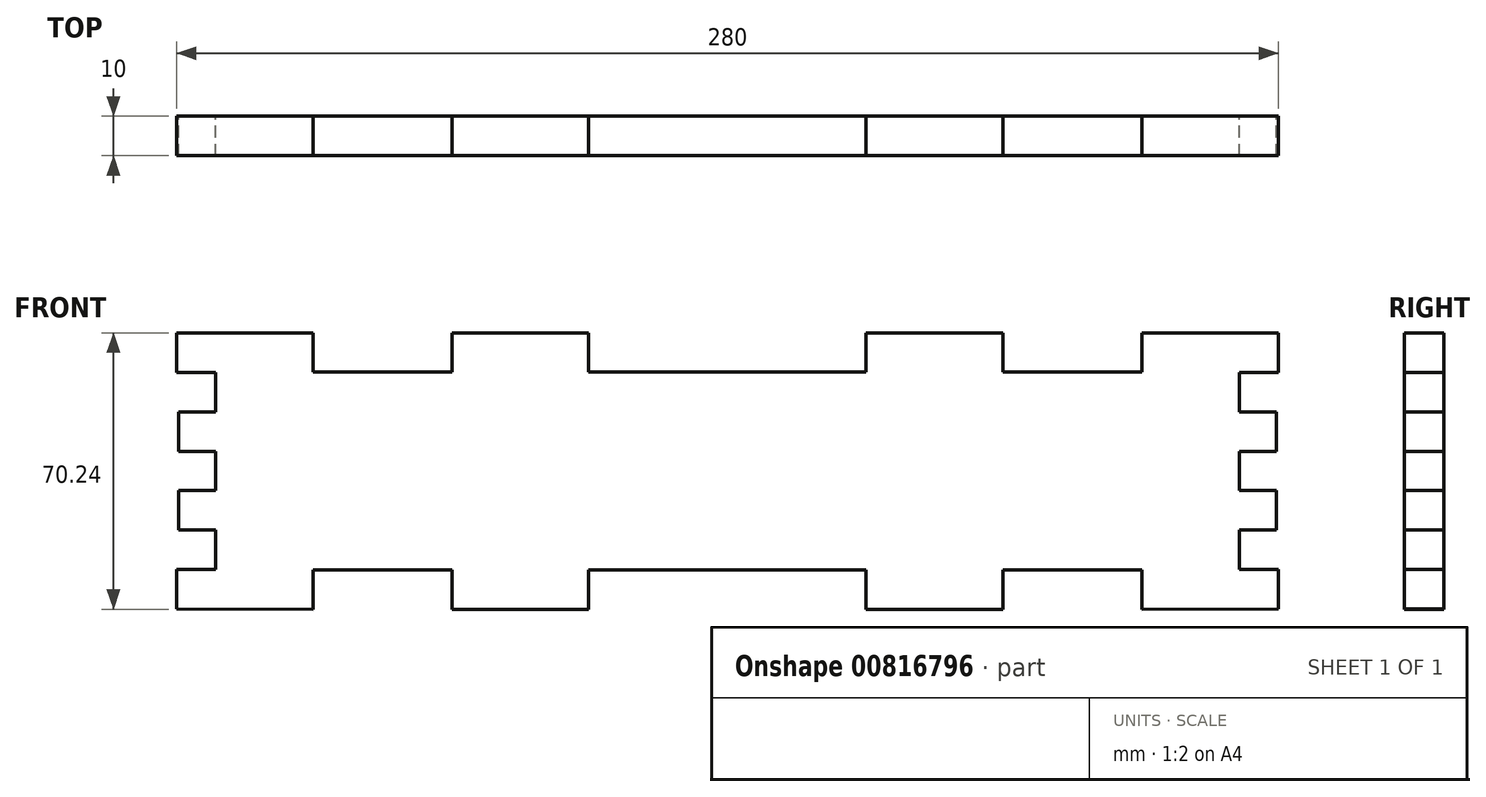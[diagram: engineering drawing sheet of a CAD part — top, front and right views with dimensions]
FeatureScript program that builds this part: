
annotation { "Feature Type Name" : "Feature", "Feature Type Description" : "" }
export const myFeature = defineFeature(function(context is Context, id is Id, definition is map)
    precondition{}
    {
        {
            var Q0;
            Q0=qCreatedBy(makeId("Front.planeOp"),FACE);
            var sketch = newSketch(context, id + "F0", { "sketchPlane" : qUnion([Q0])});
            skPoint(sketch, "E0.MirrorP", {"position": v(122.5, 95) * mm});
            skPoint(sketch, "E1.MirrorP", {"position": v(122.5, -95) * mm});
            skLineSegment(sketch, "E2", {"start": v(140, -35) * mm, "end": v(140, -25) * mm});
            skLineSegment(sketch, "E3", {"start": v(140, -25) * mm, "end": v(130, -25) * mm});
            skLineSegment(sketch, "E4", {"start": v(130, -25) * mm, "end": v(130, -15) * mm});
            skLineSegment(sketch, "E5", {"start": v(130, -15) * mm, "end": v(139.43, -15) * mm});
            skLineSegment(sketch, "E6", {"start": v(139.43, -15) * mm, "end": v(139.43, -5) * mm});
            skLineSegment(sketch, "E7", {"start": v(139.43, -5) * mm, "end": v(130, -5) * mm});
            skLineSegment(sketch, "E8.MirrorCS", {"start": v(139.43, 5) * mm, "end": v(130, 5) * mm});
            skLineSegment(sketch, "E9.MirrorCS", {"start": v(139.43, 15) * mm, "end": v(139.43, 5) * mm});
            skLineSegment(sketch, "E10.MirrorCS", {"start": v(130, 15) * mm, "end": v(139.43, 15) * mm});
            skLineSegment(sketch, "E11.MirrorCS", {"start": v(130, 25) * mm, "end": v(130, 15) * mm});
            skLineSegment(sketch, "E12.MirrorCS", {"start": v(140, 25) * mm, "end": v(130, 25) * mm});
            skLineSegment(sketch, "E13.MirrorCS", {"start": v(140, 35) * mm, "end": v(140, 25) * mm});
            skLineSegment(sketch, "E14.MirrorCS", {"start": v(-140, 35) * mm, "end": v(-140, 25) * mm});
            skLineSegment(sketch, "E15.MirrorCS", {"start": v(-140, -35) * mm, "end": v(-140, -25) * mm});
            skLineSegment(sketch, "E16.MirrorCS", {"start": v(-139.43, 15) * mm, "end": v(-139.43, 5) * mm});
            skLineSegment(sketch, "E17.MirrorCS", {"start": v(-139.43, -5) * mm, "end": v(-130, -5) * mm});
            skLineSegment(sketch, "E18.MirrorCS", {"start": v(-140, -25) * mm, "end": v(-130, -25) * mm});
            skLineSegment(sketch, "E19.MirrorCS", {"start": v(-130, -15) * mm, "end": v(-139.43, -15) * mm});
            skLineSegment(sketch, "E20.MirrorCS", {"start": v(-130, 15) * mm, "end": v(-139.43, 15) * mm});
            skLineSegment(sketch, "E21.MirrorCS", {"start": v(-140, 25) * mm, "end": v(-130, 25) * mm});
            skLineSegment(sketch, "E22.MirrorCS", {"start": v(-130, -25) * mm, "end": v(-130, -15) * mm});
            skLineSegment(sketch, "E23.MirrorCS", {"start": v(-139.43, -15) * mm, "end": v(-139.43, -5) * mm});
            skLineSegment(sketch, "E24.MirrorCS", {"start": v(-130, 25) * mm, "end": v(-130, 15) * mm});
            skLineSegment(sketch, "E25.MirrorCS", {"start": v(-139.43, 5) * mm, "end": v(-130, 5) * mm});
            skLineSegment(sketch, "E26", {"start": v(-130, 5) * mm, "end": v(-130, -5) * mm});
            skLineSegment(sketch, "E27", {"start": v(130, 5) * mm, "end": v(130, -5) * mm});
            skLineSegment(sketch, "E28", {"start": v(-140, -35) * mm, "end": v(-105.25, -35.12) * mm});
            skLineSegment(sketch, "E29", {"start": v(-105.25, -35.12) * mm, "end": v(-105.25, -25.12) * mm});
            skLineSegment(sketch, "E30", {"start": v(-105.25, -25.12) * mm, "end": v(-70, -25.12) * mm});
            skLineSegment(sketch, "E31", {"start": v(-70, -25.12) * mm, "end": v(-70, -35.12) * mm});
            skLineSegment(sketch, "E32", {"start": v(-70, -35.12) * mm, "end": v(-35.25, -35.12) * mm});
            skLineSegment(sketch, "E33", {"start": v(-35.25, -35.12) * mm, "end": v(-35.25, -25.12) * mm});
            skLineSegment(sketch, "E34", {"start": v(-35.25, -25.12) * mm, "end": v(0, -25.12) * mm});
            skLineSegment(sketch, "E35.MirrorCS", {"start": v(140, -35) * mm, "end": v(105.25, -35.12) * mm});
            skLineSegment(sketch, "E36.MirrorCS", {"start": v(105.25, -35.12) * mm, "end": v(105.25, -25.12) * mm});
            skLineSegment(sketch, "E37.MirrorCS", {"start": v(105.25, -25.12) * mm, "end": v(70, -25.12) * mm});
            skLineSegment(sketch, "E38.MirrorCS", {"start": v(70, -25.12) * mm, "end": v(70, -35.12) * mm});
            skLineSegment(sketch, "E39.MirrorCS", {"start": v(70, -35.12) * mm, "end": v(35.25, -35.12) * mm});
            skLineSegment(sketch, "E40.MirrorCS", {"start": v(35.25, -35.12) * mm, "end": v(35.25, -25.12) * mm});
            skLineSegment(sketch, "E41.MirrorCS", {"start": v(35.25, -25.12) * mm, "end": v(0, -25.12) * mm});
            skLineSegment(sketch, "E42.MirrorCS", {"start": v(-140, 35) * mm, "end": v(-105.25, 35.12) * mm});
            skLineSegment(sketch, "E43.MirrorCS", {"start": v(-105.25, 25.12) * mm, "end": v(-70, 25.12) * mm});
            skLineSegment(sketch, "E44.MirrorCS", {"start": v(-70, 25.12) * mm, "end": v(-70, 35.12) * mm});
            skLineSegment(sketch, "E45.MirrorCS", {"start": v(-105.25, 35.12) * mm, "end": v(-105.25, 25.12) * mm});
            skLineSegment(sketch, "E46.MirrorCS", {"start": v(-70, 35.12) * mm, "end": v(-35.25, 35.12) * mm});
            skLineSegment(sketch, "E47.MirrorCS", {"start": v(-35.25, 35.12) * mm, "end": v(-35.25, 25.12) * mm});
            skLineSegment(sketch, "E48.MirrorCS", {"start": v(-35.25, 25.12) * mm, "end": v(0, 25.12) * mm});
            skLineSegment(sketch, "E49.MirrorCS", {"start": v(35.25, 25.12) * mm, "end": v(0, 25.12) * mm});
            skLineSegment(sketch, "E50.MirrorCS", {"start": v(35.25, 35.12) * mm, "end": v(35.25, 25.12) * mm});
            skLineSegment(sketch, "E51.MirrorCS", {"start": v(70, 35.12) * mm, "end": v(35.25, 35.12) * mm});
            skLineSegment(sketch, "E52.MirrorCS", {"start": v(70, 25.12) * mm, "end": v(70, 35.12) * mm});
            skLineSegment(sketch, "E53.MirrorCS", {"start": v(105.25, 25.12) * mm, "end": v(70, 25.12) * mm});
            skLineSegment(sketch, "E54.MirrorCS", {"start": v(105.25, 35.12) * mm, "end": v(105.25, 25.12) * mm});
            skLineSegment(sketch, "E55.MirrorCS", {"start": v(140, 35) * mm, "end": v(105.25, 35.12) * mm});
            skSolve(sketch);
        }
        {
            var Q0;
            Q0=makeQuery(id+"F0.imprint","IMPRINT",FACE,{"disambiguationData":[TD([[makeQuery(id+"F0.imprint","IMPRINT",EDGE,{"derivedFrom":sQuery(id+"F0.wireOp",EDGE,"E2")}),1.0]])]});
            extrude(context, id + "F1", {"entities" : qUnion([Q0]), "depth" : 10 * mm, "offsetDistance" : 25 * mm});
        }
    });
